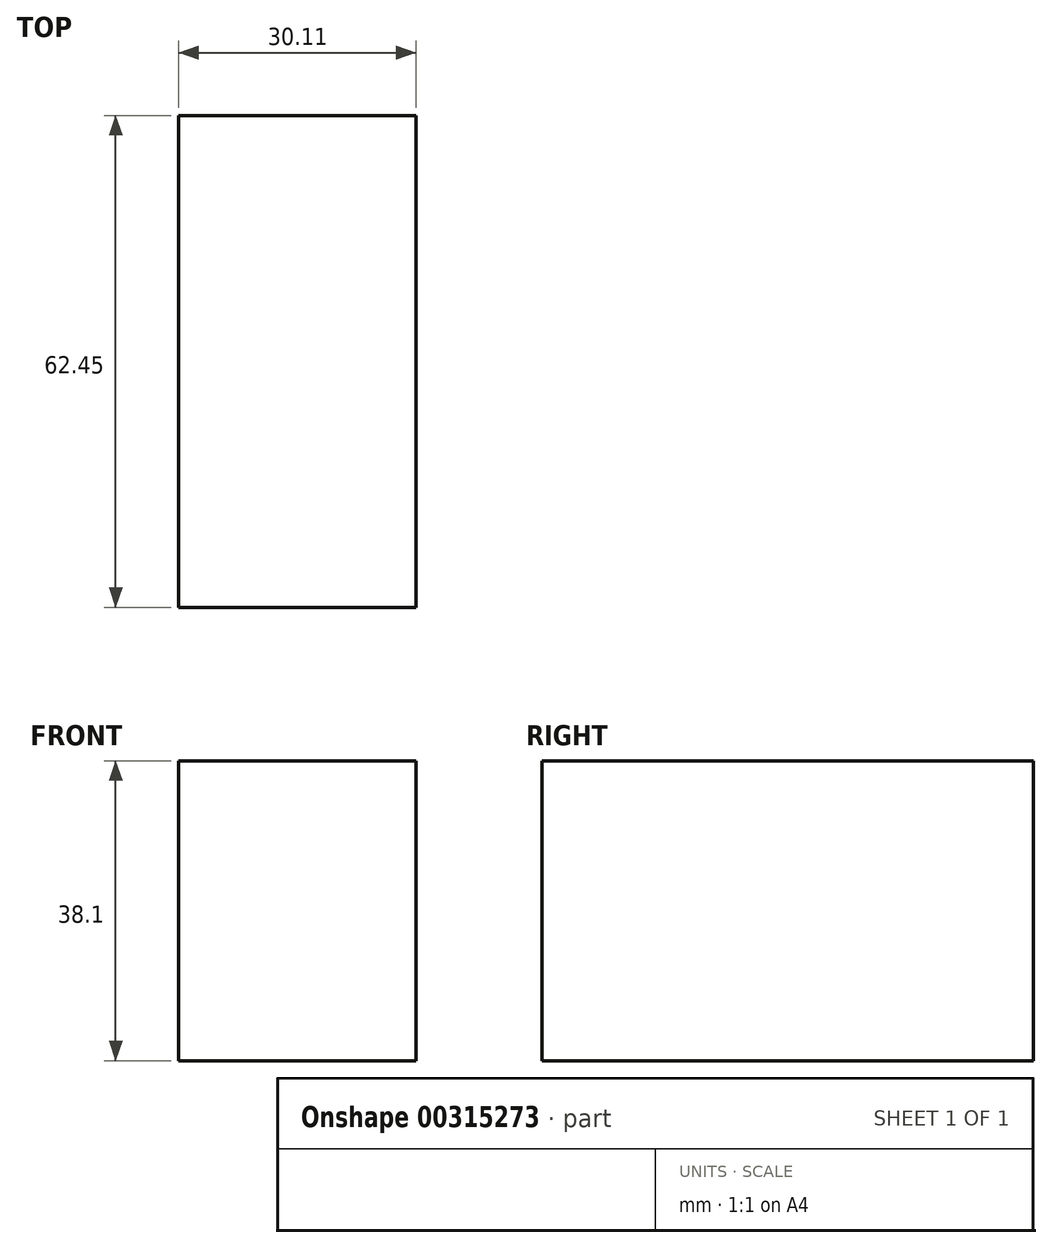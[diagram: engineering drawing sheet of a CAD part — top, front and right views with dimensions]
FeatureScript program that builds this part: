
annotation { "Feature Type Name" : "Feature", "Feature Type Description" : "" }
export const myFeature = defineFeature(function(context is Context, id is Id, definition is map)
    precondition{}
    {
        {
            var Q0;
            Q0=qCreatedBy(makeId("Top.planeOp"),FACE);
            var sketch = newSketch(context, id + "F0", { "sketchPlane" : qUnion([Q0])});
            skLineSegment(sketch, "E0.bottom", {"start": v(57.3, 0) * mm, "end": v(27.2, 0) * mm});
            skLineSegment(sketch, "E0.top", {"start": v(57.3, -62.45) * mm, "end": v(27.2, -62.45) * mm});
            skLineSegment(sketch, "E0.left", {"start": v(57.3, 0) * mm, "end": v(57.3, -62.45) * mm});
            skLineSegment(sketch, "E0.right", {"start": v(27.2, 0) * mm, "end": v(27.2, -62.45) * mm});
            skPoint(sketch, "E0.middle", {"position": v(42.26, -31.23) * mm});
            skSolve(sketch);
        }
        {
            var Q0;
            Q0 = qSketchRegion(id + "F0", true);
            extrude(context, id + "F1", {"entities" : qUnion([Q0]), "depth" : 12.7 * mm});
        }
        {
            var Q0;
            Q0=makeQuery(id+"F1.opExtrude","CAP_FACE",FACE,{"disambiguationData":[OSD([sQuery(id+"F0.wireOp",EDGE,"E0.bottom"),sQuery(id+"F0.wireOp",EDGE,"E0.top"),sQuery(id+"F0.wireOp",EDGE,"E0.left"),sQuery(id+"F0.wireOp",EDGE,"E0.right")])],"isStart":false});
            var Q1;
            Q1 = qSketchRegion(id + "F0", true);
            extrude(context, id + "F2", {"entities" : qUnion([Q0, Q1]), "operationType" : NewBodyOperationType.ADD, "depth" : 25.4 * mm});
        }
    });
